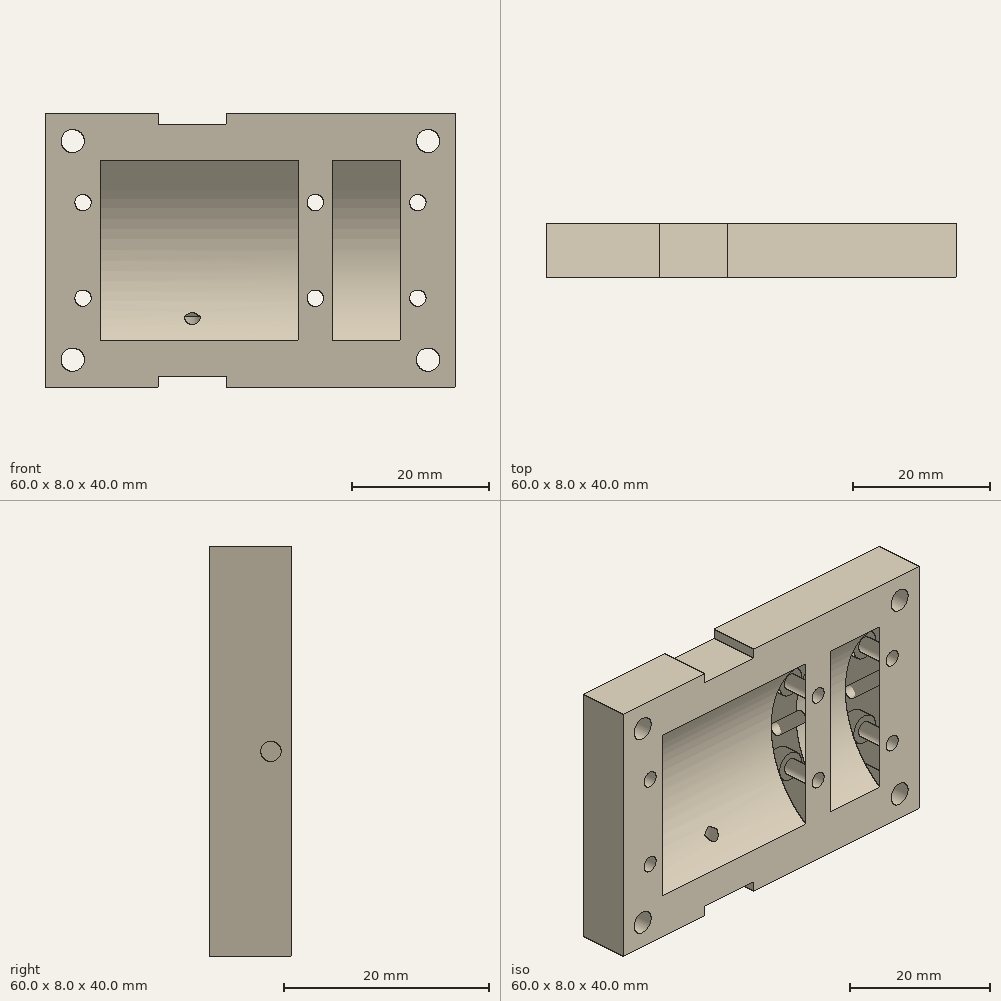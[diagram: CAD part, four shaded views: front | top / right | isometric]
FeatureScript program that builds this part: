
annotation { "Feature Type Name" : "Feature", "Feature Type Description" : "" }
export const myFeature = defineFeature(function(context is Context, id is Id, definition is map)
    precondition{}
    {
        {
            var Q0;
            Q0=qCreatedBy(makeId("Front.planeOp"),FACE);
            var sketch = newSketch(context, id + "F0", { "sketchPlane" : qUnion([Q0])});
            skLineSegment(sketch, "E0.bottom", {"start": v(0, 0) * mm, "end": v(16.5, 0) * mm});
            skLineSegment(sketch, "E0.top", {"start": v(0, 40) * mm, "end": v(16.5, 40) * mm});
            skLineSegment(sketch, "E0.left", {"start": v(0, 0) * mm, "end": v(0, 40) * mm});
            skLineSegment(sketch, "E0.right", {"start": v(60, 0) * mm, "end": v(60, 40) * mm});
            skCircle(sketch, "E1", {"center": v(4, 36) * mm, "radius": 1.7 * mm});
            skCircle(sketch, "E2", {"center": v(56, 36) * mm, "radius": 1.7 * mm});
            skCircle(sketch, "E3", {"center": v(56, 4) * mm, "radius": 1.7 * mm});
            skCircle(sketch, "E4", {"center": v(4, 4) * mm, "radius": 1.7 * mm});
            skLineSegment(sketch, "E5", {"start": v(16.5, 40) * mm, "end": v(16.5, 38.5) * mm});
            skLineSegment(sketch, "E6", {"start": v(16.5, 38.5) * mm, "end": v(26.5, 38.5) * mm});
            skLineSegment(sketch, "E7", {"start": v(26.5, 38.5) * mm, "end": v(26.5, 40) * mm});
            skLineSegment(sketch, "E8.trimOffspring", {"start": v(26.5, 40) * mm, "end": v(60, 40) * mm});
            skLineSegment(sketch, "E9", {"start": v(16.5, 0) * mm, "end": v(16.5, 1.5) * mm});
            skLineSegment(sketch, "E10", {"start": v(16.5, 1.5) * mm, "end": v(26.5, 1.5) * mm});
            skLineSegment(sketch, "E11", {"start": v(26.5, 1.5) * mm, "end": v(26.5, 0) * mm});
            skLineSegment(sketch, "E12.trimOffspring", {"start": v(26.5, 0) * mm, "end": v(60, 0) * mm});
            skSolve(sketch);
        }
        {
            var Q0;
            Q0 = qSketchRegion(id + "F0", true);
            extrude(context, id + "F1", {"entities" : qUnion([Q0]), "depth" : 8 * mm, "offsetDistance" : 25 * mm});
        }
        {
            var Q0;
            Q0=makeQuery(id+"F1.opExtrude","SWEPT_FACE",FACE,{"disambiguationData":[OSD([sQuery(id+"F0.wireOp",EDGE,"E12.trimOffspring")])]});
            var Q1;
            Q1=makeQuery(id+"F1.opExtrude","SWEPT_FACE",FACE,{"disambiguationData":[OSD([sQuery(id+"F0.wireOp",EDGE,"E8.trimOffspring")])]});
            cPlane(context, id + "F2", {"entities" : qUnion([Q0, Q1]), "cplaneType" : CPlaneType.MID_PLANE, "offset" : 25 * mm, "width" : 150 * mm, "height" : 150 * mm});
        }
        {
            var Q0;
            Q0=qCreatedBy(id+"F2.planeOp",FACE);
            var sketch = newSketch(context, id + "F3", { "sketchPlane" : qUnion([Q0])});
            skLineSegment(sketch, "E13", {"start": v(0, 17) * mm, "end": v(60, 17) * mm, "construction": true});
            skLineSegment(sketch, "E14.bottom", {"start": v(8, 17) * mm, "end": v(37, 17) * mm});
            skLineSegment(sketch, "E14.top", {"start": v(8, 1) * mm, "end": v(37, 1) * mm});
            skLineSegment(sketch, "E14.left", {"start": v(8, 1) * mm, "end": v(8, 17) * mm});
            skLineSegment(sketch, "E14.right", {"start": v(37, 1) * mm, "end": v(37, 17) * mm});
            skLineSegment(sketch, "E15.bottom", {"start": v(42, 17) * mm, "end": v(52, 17) * mm});
            skLineSegment(sketch, "E15.top", {"start": v(42, 1) * mm, "end": v(52, 1) * mm});
            skLineSegment(sketch, "E15.left", {"start": v(42, 1) * mm, "end": v(42, 17) * mm});
            skLineSegment(sketch, "E15.right", {"start": v(52, 1) * mm, "end": v(52, 17) * mm});
            skSolve(sketch);
        }
        {
            var Q0;
            Q0=makeQuery(id+"F3.imprint","IMPRINT",FACE,{"disambiguationData":[TD([[makeQuery(id+"F3.imprint","IMPRINT",EDGE,{"derivedFrom":sQuery(id+"F3.wireOp",EDGE,"E14.bottom")}),-1.0]])]});
            var Q1;
            Q1=makeQuery(id+"F3.imprint","IMPRINT",FACE,{"disambiguationData":[TD([[makeQuery(id+"F3.imprint","IMPRINT",EDGE,{"derivedFrom":sQuery(id+"F3.wireOp",EDGE,"E15.bottom")}),-1.0]])]});
            var Q2;
            Q2=sQuery(id+"F3.wireOp",EDGE,"E13");
            revolve(context, id + "F4", {"operationType" : NewBodyOperationType.REMOVE, "surfaceOperationType" : NewSurfaceOperationType.NEW, "entities" : qUnion([Q0, Q1]), "axis" : qUnion([Q2]), "revolveType" : RevolveType.FULL, "oppositeDirection" : true});
        }
        {
            var Q0;
            Q0=makeQuery(id+"F1.opExtrude","SWEPT_FACE",FACE,{"disambiguationData":[OSD([sQuery(id+"F0.wireOp",EDGE,"E10")])]});
            var sketch = newSketch(context, id + "F5", { "sketchPlane" : qUnion([Q0])});
            skPoint(sketch, "E16", {"position": v(21.5, 4) * mm});
            skSolve(sketch);
        }
        {
            var Q0;
            Q0=sQuery(id+"F5.wireOp",VERTEX,"E16");
            var Q1;
            Q1=makeQuery(id+"F1.opExtrude","SWEPT_BODY",BODY,{"disambiguationData":[OSD([sQuery(id+"F0.wireOp",EDGE,"E0.bottom"),sQuery(id+"F0.wireOp",EDGE,"E0.top"),sQuery(id+"F0.wireOp",EDGE,"E0.left"),sQuery(id+"F0.wireOp",EDGE,"E0.right"),sQuery(id+"F0.wireOp",EDGE,"E1"),sQuery(id+"F0.wireOp",EDGE,"E2"),sQuery(id+"F0.wireOp",EDGE,"E3"),sQuery(id+"F0.wireOp",EDGE,"E4"),sQuery(id+"F0.wireOp",EDGE,"E5"),sQuery(id+"F0.wireOp",EDGE,"E6"),sQuery(id+"F0.wireOp",EDGE,"E7"),sQuery(id+"F0.wireOp",EDGE,"E8.trimOffspring"),sQuery(id+"F0.wireOp",EDGE,"E9"),sQuery(id+"F0.wireOp",EDGE,"E10"),sQuery(id+"F0.wireOp",EDGE,"E11"),sQuery(id+"F0.wireOp",EDGE,"E12.trimOffspring")])]});
            hole(context, id + "F6", {"style" : HoleStyle.SIMPLE, "endStyle" : HoleEndStyle.BLIND, "standardTappedOrClearance" : lookupTablePath({ "standard" : "ISO", "engagement" : "75%", "pitch" : "0.5 mm", "size" : "M3", "type" : "Tapped" }), "standardBlindInLast" : lookupTablePath({ "standard" : "ISO", "engagement" : "75%", "pitch" : "0.5 mm", "size" : "M3", "type" : "Tapped" }), "holeDiameter" : 2.5 * mm, "majorDiameter" : 3 * mm, "showTappedDepth" : true, "holeDepth" : 8.8 * mm, "isTappedThrough" : true, "tappedDepth" : 7.3 * mm, "tapClearance" : 3, "locations" : qUnion([Q0]), "scope" : qUnion([Q1])});
        }
        {
            var Q0;
            Q0=makeQuery(id+"F1.opExtrude","SWEPT_FACE",FACE,{"disambiguationData":[OSD([sQuery(id+"F0.wireOp",EDGE,"E0.right")])]});
            var sketch = newSketch(context, id + "F7", { "sketchPlane" : qUnion([Q0])});
            skPoint(sketch, "E17", {"position": v(-2, 20) * mm});
            skSolve(sketch);
        }
        {
            var Q0;
            Q0=sQuery(id+"F7.wireOp",VERTEX,"E17");
            var Q1;
            Q1=makeQuery(id+"F1.opExtrude","SWEPT_BODY",BODY,{"disambiguationData":[OSD([sQuery(id+"F0.wireOp",EDGE,"E0.bottom"),sQuery(id+"F0.wireOp",EDGE,"E0.top"),sQuery(id+"F0.wireOp",EDGE,"E0.left"),sQuery(id+"F0.wireOp",EDGE,"E0.right"),sQuery(id+"F0.wireOp",EDGE,"E1"),sQuery(id+"F0.wireOp",EDGE,"E2"),sQuery(id+"F0.wireOp",EDGE,"E3"),sQuery(id+"F0.wireOp",EDGE,"E4"),sQuery(id+"F0.wireOp",EDGE,"E5"),sQuery(id+"F0.wireOp",EDGE,"E6"),sQuery(id+"F0.wireOp",EDGE,"E7"),sQuery(id+"F0.wireOp",EDGE,"E8.trimOffspring"),sQuery(id+"F0.wireOp",EDGE,"E9"),sQuery(id+"F0.wireOp",EDGE,"E10"),sQuery(id+"F0.wireOp",EDGE,"E11"),sQuery(id+"F0.wireOp",EDGE,"E12.trimOffspring")])]});
            hole(context, id + "F8", {"style" : HoleStyle.SIMPLE, "endStyle" : HoleEndStyle.BLIND, "standardTappedOrClearance" : lookupTablePath({ "standard" : "ISO", "size" : "2", "type" : "Drilled" }), "standardBlindInLast" : lookupTablePath({ "standard" : "ISO", "size" : "2", "type" : "Drilled" }), "holeDiameter" : 2 * mm, "majorDiameter" : 3 * mm, "holeDepth" : 40 * mm, "isTappedThrough" : true, "tappedDepth" : 7.3 * mm, "tapClearance" : 3, "locations" : qUnion([Q0]), "scope" : qUnion([Q1])});
        }
        {
            var Q0;
            Q0=makeQuery(id+"F1.opExtrude","CAP_FACE",FACE,{"disambiguationData":[OSD([sQuery(id+"F0.wireOp",EDGE,"E0.bottom"),sQuery(id+"F0.wireOp",EDGE,"E0.top"),sQuery(id+"F0.wireOp",EDGE,"E0.left"),sQuery(id+"F0.wireOp",EDGE,"E0.right"),sQuery(id+"F0.wireOp",EDGE,"E1"),sQuery(id+"F0.wireOp",EDGE,"E2"),sQuery(id+"F0.wireOp",EDGE,"E3"),sQuery(id+"F0.wireOp",EDGE,"E4"),sQuery(id+"F0.wireOp",EDGE,"E5"),sQuery(id+"F0.wireOp",EDGE,"E6"),sQuery(id+"F0.wireOp",EDGE,"E7"),sQuery(id+"F0.wireOp",EDGE,"E8.trimOffspring"),sQuery(id+"F0.wireOp",EDGE,"E9"),sQuery(id+"F0.wireOp",EDGE,"E10"),sQuery(id+"F0.wireOp",EDGE,"E11"),sQuery(id+"F0.wireOp",EDGE,"E12.trimOffspring")])],"isStart":true});
            var sketch = newSketch(context, id + "F9", { "sketchPlane" : qUnion([Q0])});
            skPoint(sketch, "E18", {"position": v(-54.5, 13) * mm});
            skPoint(sketch, "E19", {"position": v(-54.5, 27) * mm});
            skPoint(sketch, "E20", {"position": v(-39.5, 13) * mm});
            skPoint(sketch, "E21", {"position": v(-39.5, 27) * mm});
            skPoint(sketch, "E22", {"position": v(-5.5, 27) * mm});
            skPoint(sketch, "E23", {"position": v(-5.5, 13) * mm});
            skSolve(sketch);
        }
        {
            var Q0;
            Q0=sQuery(id+"F9.wireOp",VERTEX,"E18");
            var Q1;
            Q1=sQuery(id+"F9.wireOp",VERTEX,"E20");
            var Q2;
            Q2=sQuery(id+"F9.wireOp",VERTEX,"E23");
            var Q3;
            Q3=sQuery(id+"F9.wireOp",VERTEX,"E22");
            var Q4;
            Q4=sQuery(id+"F9.wireOp",VERTEX,"E21");
            var Q5;
            Q5=sQuery(id+"F9.wireOp",VERTEX,"E19");
            var Q6;
            Q6=makeQuery(id+"F1.opExtrude","SWEPT_BODY",BODY,{"disambiguationData":[OSD([sQuery(id+"F0.wireOp",EDGE,"E0.bottom"),sQuery(id+"F0.wireOp",EDGE,"E0.top"),sQuery(id+"F0.wireOp",EDGE,"E0.left"),sQuery(id+"F0.wireOp",EDGE,"E0.right"),sQuery(id+"F0.wireOp",EDGE,"E1"),sQuery(id+"F0.wireOp",EDGE,"E2"),sQuery(id+"F0.wireOp",EDGE,"E3"),sQuery(id+"F0.wireOp",EDGE,"E4"),sQuery(id+"F0.wireOp",EDGE,"E5"),sQuery(id+"F0.wireOp",EDGE,"E6"),sQuery(id+"F0.wireOp",EDGE,"E7"),sQuery(id+"F0.wireOp",EDGE,"E8.trimOffspring"),sQuery(id+"F0.wireOp",EDGE,"E9"),sQuery(id+"F0.wireOp",EDGE,"E10"),sQuery(id+"F0.wireOp",EDGE,"E11"),sQuery(id+"F0.wireOp",EDGE,"E12.trimOffspring")])]});
            hole(context, id + "F10", {"style" : HoleStyle.C_BORE, "endStyle" : HoleEndStyle.BLIND, "holeDiameter" : 2.4 * mm, "cBoreDiameter" : 4.4 * mm, "cBoreDepth" : 2.4 * mm, "majorDiameter" : 5 * mm, "holeDepth" : 40 * mm, "isTappedThrough" : true, "tappedDepth" : 7.3 * mm, "tapClearance" : 3, "locations" : qUnion([Q0, Q1, Q2, Q3, Q4, Q5]), "scope" : qUnion([Q6])});
        }
    });
